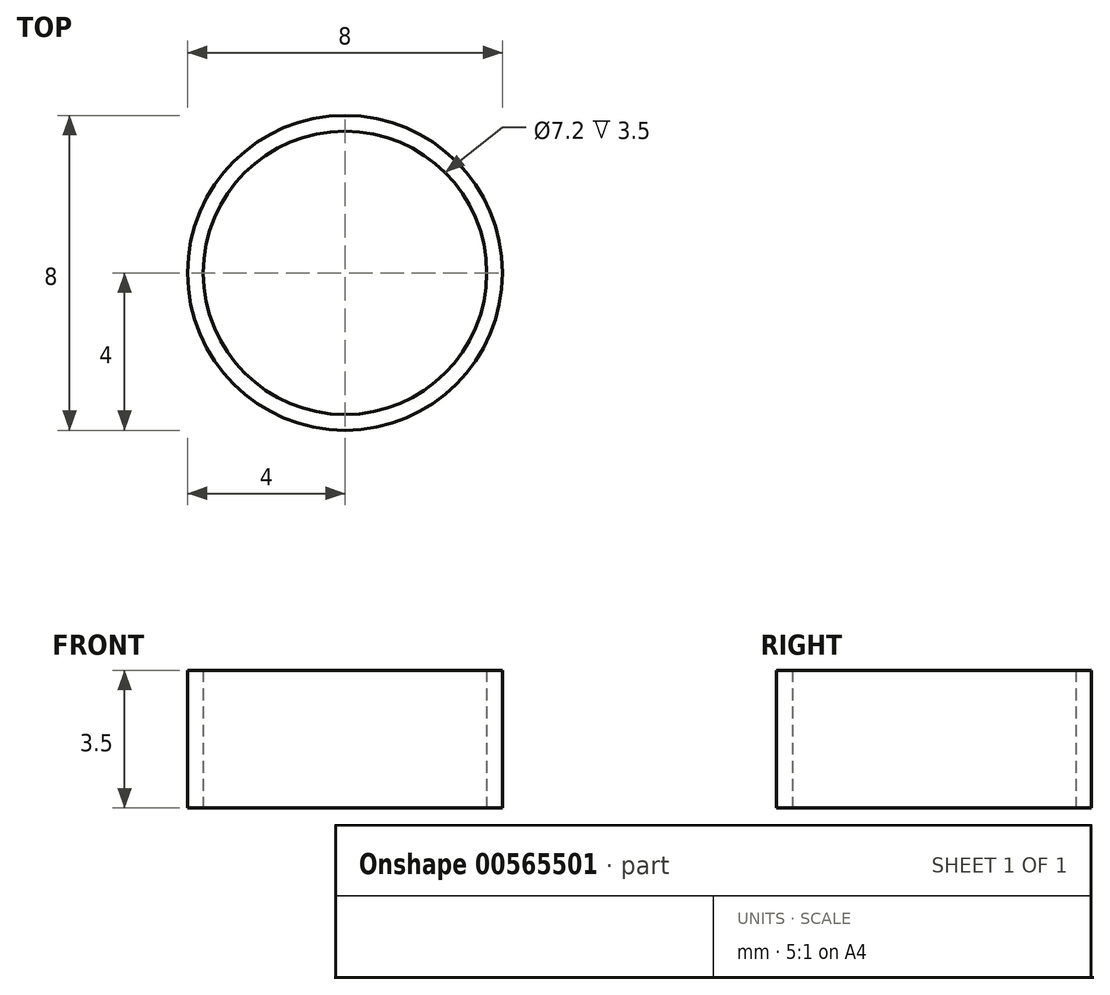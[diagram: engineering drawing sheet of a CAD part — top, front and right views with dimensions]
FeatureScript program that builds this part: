
annotation { "Feature Type Name" : "Feature", "Feature Type Description" : "" }
export const myFeature = defineFeature(function(context is Context, id is Id, definition is map)
    precondition{}
    {
        {
            var Q0;
            Q0=qCreatedBy(makeId("Top.planeOp"),FACE);
            var sketch = newSketch(context, id + "F0", { "sketchPlane" : qUnion([Q0])});
            skCircle(sketch, "E0", {"center": v(0, 0) * mm, "radius": 3.6 * mm});
            skCircle(sketch, "E1", {"center": v(0, 0) * mm, "radius": 4 * mm});
            skSolve(sketch);
        }
        {
            var Q0;
            Q0 = qSketchRegion(id + "F0", true);
            extrude(context, id + "F1", {"entities" : qUnion([Q0]), "depth" : 3.5 * mm, "offsetDistance" : 25 * mm});
        }
    });
